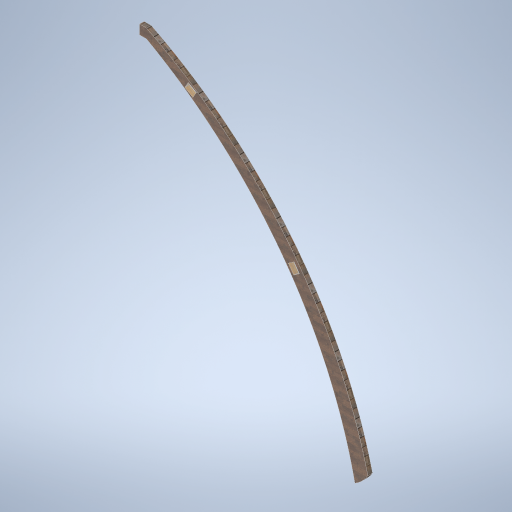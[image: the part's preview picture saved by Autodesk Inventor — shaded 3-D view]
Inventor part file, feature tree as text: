
AUTODESK INVENTOR PART (.ipt)
format: ipt  version: 2024.2 (Build 282272000, 272)  size: 310,784 bytes
history: native  units: mm
features: extrude x2, sketch x2
ambient origin geometry x8: Origin, YZ Plane, XZ Plane, XY Plane, X Axis, Y Axis, Z Axis, Center Point
bodies: Solid1 (feature_tree)
feature tree (4):
  extrude  "Extrusion1"  Depth=150.0mm
  extrude  "Extrusion2"  Depth=200.0mm
  sketch  "Sketch1"  dims[d0=9000.0mm d1=9000.0mm d2=150.0mm]
  sketch  "Sketch2"  dims[d3=100.0mm d4=0.0mm d5=200.0mm d6=30.0deg d7=150.0mm d8=200.0mm d9=9.599311mm d10=150.0mm d11=0.0mm d12=0.0mm]
